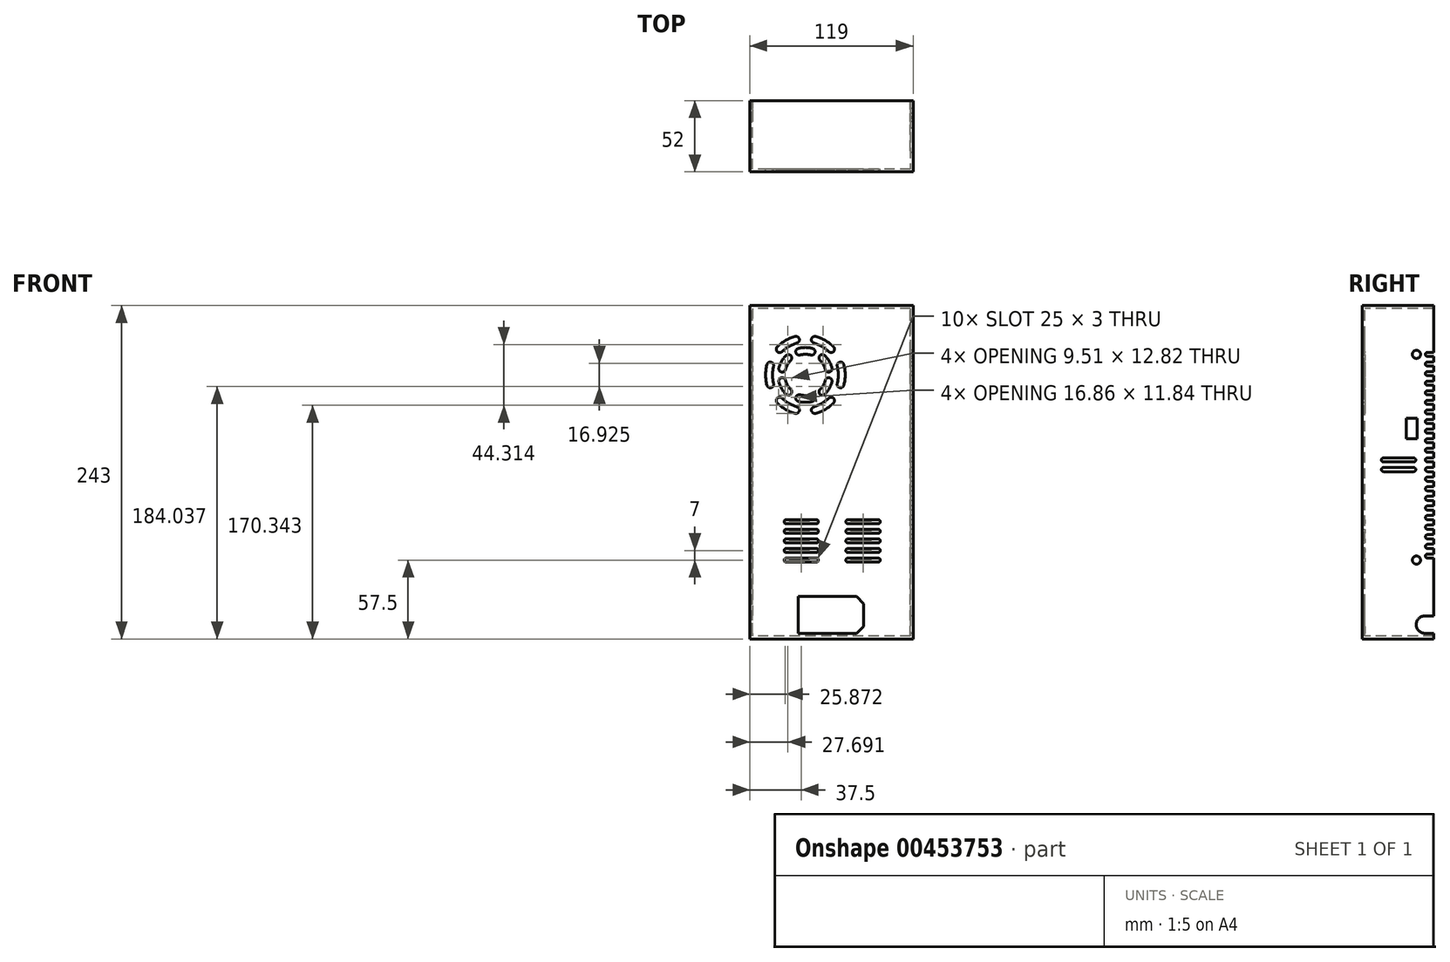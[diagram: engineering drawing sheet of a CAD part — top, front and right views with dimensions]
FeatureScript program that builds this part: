
annotation { "Feature Type Name" : "Feature", "Feature Type Description" : "" }
export const myFeature = defineFeature(function(context is Context, id is Id, definition is map)
    precondition{}
    {
        {
            assignVariable(context, id + "F0", {"name" : "Thickness", "anyValue" : 2});
        }
        {
            var Q0;
            Q0=qCreatedBy(makeId("Front.planeOp"),FACE);
            var sketch = newSketch(context, id + "F1", { "sketchPlane" : qUnion([Q0])});
            skLineSegment(sketch, "E0.bottom", {"start": v(57.5, -120.5) * mm, "end": v(-57.5, -120.5) * mm});
            skLineSegment(sketch, "E0.top", {"start": v(57.5, 120.5) * mm, "end": v(-57.5, 120.5) * mm});
            skLineSegment(sketch, "E0.left", {"start": v(57.5, -120.5) * mm, "end": v(57.5, 120.5) * mm});
            skLineSegment(sketch, "E0.right", {"start": v(-57.5, -120.5) * mm, "end": v(-57.5, 120.5) * mm});
            skPoint(sketch, "E0.middle", {"position": v(0, 0) * mm});
            skLineSegment(sketch, "E1.bottom", {"start": v(18.15, -116.5) * mm, "end": v(-24.1, -116.5) * mm});
            skLineSegment(sketch, "E1.top", {"start": v(18.15, -89.5) * mm, "end": v(-24.1, -89.5) * mm});
            skLineSegment(sketch, "E1.left", {"start": v(23.4, -111.25) * mm, "end": v(23.4, -94.75) * mm});
            skLineSegment(sketch, "E1.right", {"start": v(-24.1, -116.5) * mm, "end": v(-24.1, -89.5) * mm});
            skLineSegment(sketch, "E2", {"start": v(23.4, -94.75) * mm, "end": v(18.15, -89.5) * mm});
            skLineSegment(sketch, "E3", {"start": v(-24.1, -103) * mm, "end": v(23.75, -103) * mm, "construction": true});
            skLineSegment(sketch, "E4.MirrorCS", {"start": v(23.4, -111.25) * mm, "end": v(18.15, -116.5) * mm});
            skPoint(sketch, "E5", {"position": v(-19, 72) * mm});
            skPoint(sketch, "E6.0.6.0", {"position": v(-23.53, 55.1) * mm});
            skPoint(sketch, "E6.0.7.0", {"position": v(-14.47, 55.1) * mm});
            skArc(sketch, "E7", {"start": v(-14.47, 55.1) * mm, "mid": v(-19, 54.5) * mm, "end": v(-23.53, 55.1) * mm, "construction": true});
            skPoint(sketch, "E8", {"position": v(-12.14, 97.6) * mm});
            skPoint(sketch, "E9.0.11.0", {"position": v(-0.26, 90.74) * mm});
            skArc(sketch, "E10", {"start": v(-12.14, 97.6) * mm, "mid": v(-5.75, 94.95) * mm, "end": v(-0.26, 90.74) * mm, "construction": true});
            skArc(sketch, "E11.1.startCap", {"start": v(-12.79, 95.18) * mm, "mid": v(-14.56, 98.24) * mm, "end": v(-11.5, 100.01) * mm});
            skArc(sketch, "E11.1.endCap", {"start": v(1.5, 92.5) * mm, "mid": v(1.5, 88.97) * mm, "end": v(-2.03, 88.97) * mm});
            skArc(sketch, "E11.1.left", {"start": v(-11.5, 100.01) * mm, "mid": v(-4.5, 97.11) * mm, "end": v(1.5, 92.5) * mm});
            skArc(sketch, "E11.1.right", {"start": v(-12.79, 95.18) * mm, "mid": v(-7, 92.78) * mm, "end": v(-2.03, 88.97) * mm});
            skArc(sketch, "E11.10.startCap", {"start": v(-15.12, 57.51) * mm, "mid": v(-12.06, 55.74) * mm, "end": v(-13.82, 52.68) * mm});
            skArc(sketch, "E11.10.endCap", {"start": v(-24.18, 52.68) * mm, "mid": v(-25.94, 55.74) * mm, "end": v(-22.88, 57.51) * mm});
            skArc(sketch, "E11.10.left", {"start": v(-13.82, 52.68) * mm, "mid": v(-19, 52) * mm, "end": v(-24.18, 52.68) * mm});
            skArc(sketch, "E11.10.right", {"start": v(-15.12, 57.51) * mm, "mid": v(-19, 57) * mm, "end": v(-22.88, 57.51) * mm});
            skLineSegment(sketch, "E12", {"start": v(-33, -35) * mm, "end": v(-11, -35) * mm, "construction": true});
            skArc(sketch, "E13.0.startCap", {"start": v(-33, -36.5) * mm, "mid": v(-34.5, -35) * mm, "end": v(-33, -33.5) * mm});
            skArc(sketch, "E13.0.endCap", {"start": v(-11, -33.5) * mm, "mid": v(-9.5, -35) * mm, "end": v(-11, -36.5) * mm});
            skLineSegment(sketch, "E13.0.left", {"start": v(-33, -33.5) * mm, "end": v(-11, -33.5) * mm});
            skLineSegment(sketch, "E13.0.right", {"start": v(-33, -36.5) * mm, "end": v(-11, -36.5) * mm});
            skLineSegment(sketch, "E14.0.1.0", {"start": v(-33, -43.5) * mm, "end": v(-11, -43.5) * mm});
            skArc(sketch, "E14.0.1.1", {"start": v(-33, -43.5) * mm, "mid": v(-34.5, -42) * mm, "end": v(-33, -40.5) * mm});
            skLineSegment(sketch, "E14.0.1.2", {"start": v(-33, -40.5) * mm, "end": v(-11, -40.5) * mm});
            skArc(sketch, "E14.0.1.3", {"start": v(-11, -40.5) * mm, "mid": v(-9.5, -42) * mm, "end": v(-11, -43.5) * mm});
            skLineSegment(sketch, "E14.0.2.0", {"start": v(-33, -50.5) * mm, "end": v(-11, -50.5) * mm});
            skArc(sketch, "E14.0.2.1", {"start": v(-33, -50.5) * mm, "mid": v(-34.5, -49) * mm, "end": v(-33, -47.5) * mm});
            skLineSegment(sketch, "E14.0.2.2", {"start": v(-33, -47.5) * mm, "end": v(-11, -47.5) * mm});
            skArc(sketch, "E14.0.2.3", {"start": v(-11, -47.5) * mm, "mid": v(-9.5, -49) * mm, "end": v(-11, -50.5) * mm});
            skLineSegment(sketch, "E14.0.3.0", {"start": v(-33, -57.5) * mm, "end": v(-11, -57.5) * mm});
            skArc(sketch, "E14.0.3.1", {"start": v(-33, -57.5) * mm, "mid": v(-34.5, -56) * mm, "end": v(-33, -54.5) * mm});
            skLineSegment(sketch, "E14.0.3.2", {"start": v(-33, -54.5) * mm, "end": v(-11, -54.5) * mm});
            skArc(sketch, "E14.0.3.3", {"start": v(-11, -54.5) * mm, "mid": v(-9.5, -56) * mm, "end": v(-11, -57.5) * mm});
            skLineSegment(sketch, "E14.0.4.0", {"start": v(-33, -64.5) * mm, "end": v(-11, -64.5) * mm});
            skArc(sketch, "E14.0.4.1", {"start": v(-33, -64.5) * mm, "mid": v(-34.5, -63) * mm, "end": v(-33, -61.5) * mm});
            skLineSegment(sketch, "E14.0.4.2", {"start": v(-33, -61.5) * mm, "end": v(-11, -61.5) * mm});
            skArc(sketch, "E14.0.4.3", {"start": v(-11, -61.5) * mm, "mid": v(-9.5, -63) * mm, "end": v(-11, -64.5) * mm});
            skLineSegment(sketch, "E14.1.0.0", {"start": v(12, -36.5) * mm, "end": v(34, -36.5) * mm});
            skArc(sketch, "E14.1.0.1", {"start": v(12, -36.5) * mm, "mid": v(10.5, -35) * mm, "end": v(12, -33.5) * mm});
            skLineSegment(sketch, "E14.1.0.2", {"start": v(12, -33.5) * mm, "end": v(34, -33.5) * mm});
            skArc(sketch, "E14.1.0.3", {"start": v(34, -33.5) * mm, "mid": v(35.5, -35) * mm, "end": v(34, -36.5) * mm});
            skLineSegment(sketch, "E14.1.1.0", {"start": v(12, -43.5) * mm, "end": v(34, -43.5) * mm});
            skArc(sketch, "E14.1.1.1", {"start": v(12, -43.5) * mm, "mid": v(10.5, -42) * mm, "end": v(12, -40.5) * mm});
            skLineSegment(sketch, "E14.1.1.2", {"start": v(12, -40.5) * mm, "end": v(34, -40.5) * mm});
            skArc(sketch, "E14.1.1.3", {"start": v(34, -40.5) * mm, "mid": v(35.5, -42) * mm, "end": v(34, -43.5) * mm});
            skLineSegment(sketch, "E14.1.2.0", {"start": v(12, -50.5) * mm, "end": v(34, -50.5) * mm});
            skArc(sketch, "E14.1.2.1", {"start": v(12, -50.5) * mm, "mid": v(10.5, -49) * mm, "end": v(12, -47.5) * mm});
            skLineSegment(sketch, "E14.1.2.2", {"start": v(12, -47.5) * mm, "end": v(34, -47.5) * mm});
            skArc(sketch, "E14.1.2.3", {"start": v(34, -47.5) * mm, "mid": v(35.5, -49) * mm, "end": v(34, -50.5) * mm});
            skLineSegment(sketch, "E14.1.3.0", {"start": v(12, -57.5) * mm, "end": v(34, -57.5) * mm});
            skArc(sketch, "E14.1.3.1", {"start": v(12, -57.5) * mm, "mid": v(10.5, -56) * mm, "end": v(12, -54.5) * mm});
            skLineSegment(sketch, "E14.1.3.2", {"start": v(12, -54.5) * mm, "end": v(34, -54.5) * mm});
            skArc(sketch, "E14.1.3.3", {"start": v(34, -54.5) * mm, "mid": v(35.5, -56) * mm, "end": v(34, -57.5) * mm});
            skLineSegment(sketch, "E14.1.4.0", {"start": v(12, -64.5) * mm, "end": v(34, -64.5) * mm});
            skArc(sketch, "E14.1.4.1", {"start": v(12, -64.5) * mm, "mid": v(10.5, -63) * mm, "end": v(12, -61.5) * mm});
            skLineSegment(sketch, "E14.1.4.2", {"start": v(12, -61.5) * mm, "end": v(34, -61.5) * mm});
            skArc(sketch, "E14.1.4.3", {"start": v(34, -61.5) * mm, "mid": v(35.5, -63) * mm, "end": v(34, -64.5) * mm});
            skLineSegment(sketch, "E14.direction1", {"start": v(-33, -36.5) * mm, "end": v(12, -36.5) * mm, "construction": true});
            skLineSegment(sketch, "E14.direction2", {"start": v(-33, -36.5) * mm, "end": v(-33, -43.5) * mm, "construction": true});
            skLineSegment(sketch, "E15", {"start": v(-19, 72) * mm, "end": v(-12.14, 97.6) * mm, "construction": true});
            skLineSegment(sketch, "E16", {"start": v(-19, 72) * mm, "end": v(-19, 89.5) * mm, "construction": true});
            skLineSegment(sketch, "E17", {"start": v(-19, 72) * mm, "end": v(-0.26, 90.74) * mm, "construction": true});
            skLineSegment(sketch, "E18", {"start": v(-19, 72) * mm, "end": v(-14.47, 55.1) * mm, "construction": true});
            skLineSegment(sketch, "E19", {"start": v(-19, 72) * mm, "end": v(-23.53, 55.1) * mm, "construction": true});
            skLineSegment(sketch, "E20", {"start": v(-19, 72) * mm, "end": v(-19, 54.5) * mm, "construction": true});
            skArc(sketch, "E21.1.0", {"start": v(-39.5, 92.5) * mm, "mid": v(-33.5, 97.11) * mm, "end": v(-26.5, 100.01) * mm});
            skArc(sketch, "E21.1.1", {"start": v(-26.5, 100.01) * mm, "mid": v(-23.44, 98.24) * mm, "end": v(-25.21, 95.18) * mm});
            skArc(sketch, "E21.1.2", {"start": v(-35.97, 88.97) * mm, "mid": v(-31, 92.78) * mm, "end": v(-25.21, 95.18) * mm});
            skArc(sketch, "E21.1.3", {"start": v(-35.97, 88.97) * mm, "mid": v(-39.5, 88.97) * mm, "end": v(-39.5, 92.5) * mm});
            skArc(sketch, "E21.1.4", {"start": v(-4.51, 68.12) * mm, "mid": v(-6, 64.5) * mm, "end": v(-8.4, 61.4) * mm});
            skArc(sketch, "E21.1.5", {"start": v(0.32, 66.82) * mm, "mid": v(-1.68, 62) * mm, "end": v(-4.86, 57.86) * mm});
            skArc(sketch, "E21.1.6", {"start": v(-4.86, 57.86) * mm, "mid": v(-8.4, 57.86) * mm, "end": v(-8.4, 61.4) * mm});
            skArc(sketch, "E21.1.7", {"start": v(-4.51, 68.12) * mm, "mid": v(-1.45, 69.89) * mm, "end": v(0.32, 66.82) * mm});
            skArc(sketch, "E21.2.0", {"start": v(-47.01, 64.5) * mm, "mid": v(-48, 72) * mm, "end": v(-47.01, 79.5) * mm});
            skArc(sketch, "E21.2.1", {"start": v(-47.01, 79.5) * mm, "mid": v(-43.95, 81.27) * mm, "end": v(-42.18, 78.21) * mm});
            skArc(sketch, "E21.2.2", {"start": v(-42.18, 65.79) * mm, "mid": v(-43, 72) * mm, "end": v(-42.18, 78.21) * mm});
            skArc(sketch, "E21.2.3", {"start": v(-42.18, 65.79) * mm, "mid": v(-43.95, 62.73) * mm, "end": v(-47.01, 64.5) * mm});
            skArc(sketch, "E21.2.4", {"start": v(-8.4, 82.6) * mm, "mid": v(-6, 79.5) * mm, "end": v(-4.51, 75.88) * mm});
            skArc(sketch, "E21.2.5", {"start": v(-4.86, 86.14) * mm, "mid": v(-1.68, 82) * mm, "end": v(0.32, 77.18) * mm});
            skArc(sketch, "E21.2.6", {"start": v(0.32, 77.18) * mm, "mid": v(-1.45, 74.11) * mm, "end": v(-4.51, 75.88) * mm});
            skArc(sketch, "E21.2.7", {"start": v(-8.4, 82.6) * mm, "mid": v(-8.4, 86.14) * mm, "end": v(-4.86, 86.14) * mm});
            skArc(sketch, "E21.3.0", {"start": v(-26.5, 43.99) * mm, "mid": v(-33.5, 46.89) * mm, "end": v(-39.5, 51.5) * mm});
            skArc(sketch, "E21.3.1", {"start": v(-39.5, 51.5) * mm, "mid": v(-39.5, 55.03) * mm, "end": v(-35.97, 55.03) * mm});
            skArc(sketch, "E21.3.2", {"start": v(-25.21, 48.82) * mm, "mid": v(-31, 51.22) * mm, "end": v(-35.97, 55.03) * mm});
            skArc(sketch, "E21.3.3", {"start": v(-25.21, 48.82) * mm, "mid": v(-23.44, 45.76) * mm, "end": v(-26.5, 43.99) * mm});
            skArc(sketch, "E21.3.4", {"start": v(-22.88, 86.49) * mm, "mid": v(-19, 87) * mm, "end": v(-15.12, 86.49) * mm});
            skArc(sketch, "E21.3.5", {"start": v(-24.18, 91.32) * mm, "mid": v(-19, 92) * mm, "end": v(-13.82, 91.32) * mm});
            skArc(sketch, "E21.3.6", {"start": v(-13.82, 91.32) * mm, "mid": v(-12.06, 88.26) * mm, "end": v(-15.12, 86.49) * mm});
            skArc(sketch, "E21.3.7", {"start": v(-22.88, 86.49) * mm, "mid": v(-25.94, 88.26) * mm, "end": v(-24.18, 91.32) * mm});
            skArc(sketch, "E21.4.0", {"start": v(1.5, 51.5) * mm, "mid": v(-4.5, 46.89) * mm, "end": v(-11.5, 43.99) * mm});
            skArc(sketch, "E21.4.1", {"start": v(-11.5, 43.99) * mm, "mid": v(-14.56, 45.76) * mm, "end": v(-12.79, 48.82) * mm});
            skArc(sketch, "E21.4.2", {"start": v(-2.03, 55.03) * mm, "mid": v(-7, 51.22) * mm, "end": v(-12.79, 48.82) * mm});
            skArc(sketch, "E21.4.3", {"start": v(-2.03, 55.03) * mm, "mid": v(1.5, 55.03) * mm, "end": v(1.5, 51.5) * mm});
            skArc(sketch, "E21.4.4", {"start": v(-33.49, 75.88) * mm, "mid": v(-32, 79.5) * mm, "end": v(-29.6, 82.6) * mm});
            skArc(sketch, "E21.4.5", {"start": v(-38.32, 77.18) * mm, "mid": v(-36.32, 82) * mm, "end": v(-33.14, 86.14) * mm});
            skArc(sketch, "E21.4.6", {"start": v(-33.14, 86.14) * mm, "mid": v(-29.6, 86.14) * mm, "end": v(-29.6, 82.6) * mm});
            skArc(sketch, "E21.4.7", {"start": v(-33.49, 75.88) * mm, "mid": v(-36.55, 74.11) * mm, "end": v(-38.32, 77.18) * mm});
            skArc(sketch, "E21.5.0", {"start": v(9.01, 79.5) * mm, "mid": v(10, 72) * mm, "end": v(9.01, 64.5) * mm});
            skArc(sketch, "E21.5.1", {"start": v(9.01, 64.5) * mm, "mid": v(5.95, 62.73) * mm, "end": v(4.18, 65.79) * mm});
            skArc(sketch, "E21.5.2", {"start": v(4.18, 78.21) * mm, "mid": v(5, 72) * mm, "end": v(4.18, 65.79) * mm});
            skArc(sketch, "E21.5.3", {"start": v(4.18, 78.21) * mm, "mid": v(5.95, 81.27) * mm, "end": v(9.01, 79.5) * mm});
            skArc(sketch, "E21.5.4", {"start": v(-29.6, 61.4) * mm, "mid": v(-32, 64.5) * mm, "end": v(-33.49, 68.12) * mm});
            skArc(sketch, "E21.5.5", {"start": v(-33.14, 57.86) * mm, "mid": v(-36.32, 62) * mm, "end": v(-38.32, 66.82) * mm});
            skArc(sketch, "E21.5.6", {"start": v(-38.32, 66.82) * mm, "mid": v(-36.55, 69.89) * mm, "end": v(-33.49, 68.12) * mm});
            skArc(sketch, "E21.5.7", {"start": v(-29.6, 61.4) * mm, "mid": v(-29.6, 57.86) * mm, "end": v(-33.14, 57.86) * mm});
            skSolve(sketch);
        }
        {
            var Q0;
            Q0=makeQuery(id+"F1.imprint","IMPRINT",FACE,{"disambiguationData":[TD([[makeQuery(id+"F1.imprint","IMPRINT",EDGE,{"derivedFrom":sQuery(id+"F1.wireOp",EDGE,"E0.bottom")}),-1.0]])]});
            extrude(context, id + "F2", {"entities" : qUnion([Q0]), "depth" : (getVariable(context, 'Thickness')) * mm});
        }
        {
            var Q0;
            Q0=makeQuery(id+"F2.opExtrude","SWEPT_FACE",FACE,{"disambiguationData":[OSD([sQuery(id+"F1.wireOp",EDGE,"E0.left")])]});
            var sketch = newSketch(context, id + "F3", { "sketchPlane" : qUnion([Q0])});
            skLineSegment(sketch, "E22.bottom", {"start": v(50, 120.5) * mm, "end": v(-2, 120.5) * mm});
            skLineSegment(sketch, "E22.top", {"start": v(50, -120.5) * mm, "end": v(-2, -120.5) * mm});
            skLineSegment(sketch, "E22.left", {"start": v(50, 120.5) * mm, "end": v(50, -120.5) * mm});
            skLineSegment(sketch, "E22.right", {"start": v(-2, 120.5) * mm, "end": v(-2, -120.5) * mm});
            skCircle(sketch, "E23", {"center": v(37.5, 87) * mm, "radius": 3 * mm});
            skCircle(sketch, "E24", {"center": v(37.5, -63) * mm, "radius": 3 * mm});
            skLineSegment(sketch, "E25.bottom", {"start": v(38, 40.5) * mm, "end": v(30, 40.5) * mm});
            skLineSegment(sketch, "E25.top", {"start": v(38, 25.5) * mm, "end": v(30, 25.5) * mm});
            skLineSegment(sketch, "E25.left", {"start": v(38, 40.5) * mm, "end": v(38, 25.5) * mm});
            skLineSegment(sketch, "E25.right", {"start": v(30, 40.5) * mm, "end": v(30, 25.5) * mm});
            skLineSegment(sketch, "E26", {"start": v(50, -120.5) * mm, "end": v(50, -120.5) * mm});
            skPoint(sketch, "E27", {"position": v(50, -110) * mm});
            skLineSegment(sketch, "E28", {"start": v(43.65, -103.65) * mm, "end": v(50, -103.65) * mm});
            skLineSegment(sketch, "E29", {"start": v(43.65, -116.35) * mm, "end": v(50, -116.35) * mm});
            skArc(sketch, "E30", {"start": v(43.65, -103.65) * mm, "mid": v(37.3, -110) * mm, "end": v(43.65, -116.35) * mm});
            skArc(sketch, "E31", {"start": v(43.65, -116.35) * mm, "mid": v(50, -110) * mm, "end": v(43.65, -103.65) * mm, "construction": true});
            skLineSegment(sketch, "E32", {"start": v(13.5, 10) * mm, "end": v(35.5, 10) * mm});
            skArc(sketch, "E33.0.startCap", {"start": v(13.5, 8.5) * mm, "mid": v(12, 10) * mm, "end": v(13.5, 11.5) * mm});
            skArc(sketch, "E33.0.endCap", {"start": v(35.5, 11.5) * mm, "mid": v(37, 10) * mm, "end": v(35.5, 8.5) * mm});
            skLineSegment(sketch, "E33.0.left", {"start": v(13.5, 11.5) * mm, "end": v(35.5, 11.5) * mm});
            skLineSegment(sketch, "E33.0.right", {"start": v(13.5, 8.5) * mm, "end": v(35.5, 8.5) * mm});
            skLineSegment(sketch, "E34.0.1.0", {"start": v(13.5, 4.5) * mm, "end": v(35.5, 4.5) * mm});
            skLineSegment(sketch, "E34.0.1.1", {"start": v(13.5, 1.5) * mm, "end": v(35.5, 1.5) * mm});
            skArc(sketch, "E34.0.1.2", {"start": v(13.5, 1.5) * mm, "mid": v(12, 3) * mm, "end": v(13.5, 4.5) * mm});
            skArc(sketch, "E34.0.1.3", {"start": v(35.5, 4.5) * mm, "mid": v(37, 3) * mm, "end": v(35.5, 1.5) * mm});
            skLineSegment(sketch, "E34.direction1", {"start": v(13.5, 11.5) * mm, "end": v(35.5, 11.5) * mm, "construction": true});
            skLineSegment(sketch, "E34.direction2", {"start": v(13.5, 11.5) * mm, "end": v(13.5, 4.5) * mm, "construction": true});
            skLineSegment(sketch, "E35", {"start": v(50, 87) * mm, "end": v(45.5, 87) * mm, "construction": true});
            skArc(sketch, "E36.0.endCap", {"start": v(45.5, 85.5) * mm, "mid": v(44, 87) * mm, "end": v(45.5, 88.5) * mm});
            skLineSegment(sketch, "E36.0.left", {"start": v(50, 85.5) * mm, "end": v(45.5, 85.5) * mm});
            skLineSegment(sketch, "E36.0.right", {"start": v(50, 88.5) * mm, "end": v(45.5, 88.5) * mm});
            skLineSegment(sketch, "E37.0.1.0", {"start": v(50, 81.5) * mm, "end": v(45.5, 81.5) * mm});
            skLineSegment(sketch, "E37.0.1.1", {"start": v(50, 78.5) * mm, "end": v(45.5, 78.5) * mm});
            skArc(sketch, "E37.0.1.2", {"start": v(45.5, 78.5) * mm, "mid": v(44, 80) * mm, "end": v(45.5, 81.5) * mm});
            skLineSegment(sketch, "E37.0.2.0", {"start": v(50, 74.5) * mm, "end": v(45.5, 74.5) * mm});
            skLineSegment(sketch, "E37.0.2.1", {"start": v(50, 71.5) * mm, "end": v(45.5, 71.5) * mm});
            skArc(sketch, "E37.0.2.2", {"start": v(45.5, 71.5) * mm, "mid": v(44, 73) * mm, "end": v(45.5, 74.5) * mm});
            skLineSegment(sketch, "E37.0.3.0", {"start": v(50, 67.5) * mm, "end": v(45.5, 67.5) * mm});
            skLineSegment(sketch, "E37.0.3.1", {"start": v(50, 64.5) * mm, "end": v(45.5, 64.5) * mm});
            skArc(sketch, "E37.0.3.2", {"start": v(45.5, 64.5) * mm, "mid": v(44, 66) * mm, "end": v(45.5, 67.5) * mm});
            skLineSegment(sketch, "E37.0.4.0", {"start": v(50, 60.5) * mm, "end": v(45.5, 60.5) * mm});
            skLineSegment(sketch, "E37.0.4.1", {"start": v(50, 57.5) * mm, "end": v(45.5, 57.5) * mm});
            skArc(sketch, "E37.0.4.2", {"start": v(45.5, 57.5) * mm, "mid": v(44, 59) * mm, "end": v(45.5, 60.5) * mm});
            skLineSegment(sketch, "E37.0.5.0", {"start": v(50, 53.5) * mm, "end": v(45.5, 53.5) * mm});
            skLineSegment(sketch, "E37.0.5.1", {"start": v(50, 50.5) * mm, "end": v(45.5, 50.5) * mm});
            skArc(sketch, "E37.0.5.2", {"start": v(45.5, 50.5) * mm, "mid": v(44, 52) * mm, "end": v(45.5, 53.5) * mm});
            skLineSegment(sketch, "E37.0.6.0", {"start": v(50, 46.5) * mm, "end": v(45.5, 46.5) * mm});
            skLineSegment(sketch, "E37.0.6.1", {"start": v(50, 43.5) * mm, "end": v(45.5, 43.5) * mm});
            skArc(sketch, "E37.0.6.2", {"start": v(45.5, 43.5) * mm, "mid": v(44, 45) * mm, "end": v(45.5, 46.5) * mm});
            skLineSegment(sketch, "E37.0.7.0", {"start": v(50, 39.5) * mm, "end": v(45.5, 39.5) * mm});
            skLineSegment(sketch, "E37.0.7.1", {"start": v(50, 36.5) * mm, "end": v(45.5, 36.5) * mm});
            skArc(sketch, "E37.0.7.2", {"start": v(45.5, 36.5) * mm, "mid": v(44, 38) * mm, "end": v(45.5, 39.5) * mm});
            skLineSegment(sketch, "E37.0.8.0", {"start": v(50, 32.5) * mm, "end": v(45.5, 32.5) * mm});
            skLineSegment(sketch, "E37.0.8.1", {"start": v(50, 29.5) * mm, "end": v(45.5, 29.5) * mm});
            skArc(sketch, "E37.0.8.2", {"start": v(45.5, 29.5) * mm, "mid": v(44, 31) * mm, "end": v(45.5, 32.5) * mm});
            skLineSegment(sketch, "E37.0.9.0", {"start": v(50, 25.5) * mm, "end": v(45.5, 25.5) * mm});
            skLineSegment(sketch, "E37.0.9.1", {"start": v(50, 22.5) * mm, "end": v(45.5, 22.5) * mm});
            skArc(sketch, "E37.0.9.2", {"start": v(45.5, 22.5) * mm, "mid": v(44, 24) * mm, "end": v(45.5, 25.5) * mm});
            skLineSegment(sketch, "E37.0.10.0", {"start": v(50, 18.5) * mm, "end": v(45.5, 18.5) * mm});
            skLineSegment(sketch, "E37.0.10.1", {"start": v(50, 15.5) * mm, "end": v(45.5, 15.5) * mm});
            skArc(sketch, "E37.0.10.2", {"start": v(45.5, 15.5) * mm, "mid": v(44, 17) * mm, "end": v(45.5, 18.5) * mm});
            skLineSegment(sketch, "E37.0.11.0", {"start": v(50, 11.5) * mm, "end": v(45.5, 11.5) * mm});
            skLineSegment(sketch, "E37.0.11.1", {"start": v(50, 8.5) * mm, "end": v(45.5, 8.5) * mm});
            skArc(sketch, "E37.0.11.2", {"start": v(45.5, 8.5) * mm, "mid": v(44, 10) * mm, "end": v(45.5, 11.5) * mm});
            skLineSegment(sketch, "E37.0.12.0", {"start": v(50, 4.5) * mm, "end": v(45.5, 4.5) * mm});
            skLineSegment(sketch, "E37.0.12.1", {"start": v(50, 1.5) * mm, "end": v(45.5, 1.5) * mm});
            skArc(sketch, "E37.0.12.2", {"start": v(45.5, 1.5) * mm, "mid": v(44, 3) * mm, "end": v(45.5, 4.5) * mm});
            skLineSegment(sketch, "E37.0.13.0", {"start": v(50, -2.5) * mm, "end": v(45.5, -2.5) * mm});
            skLineSegment(sketch, "E37.0.13.1", {"start": v(50, -5.5) * mm, "end": v(45.5, -5.5) * mm});
            skArc(sketch, "E37.0.13.2", {"start": v(45.5, -5.5) * mm, "mid": v(44, -4) * mm, "end": v(45.5, -2.5) * mm});
            skLineSegment(sketch, "E37.0.14.0", {"start": v(50, -9.5) * mm, "end": v(45.5, -9.5) * mm});
            skLineSegment(sketch, "E37.0.14.1", {"start": v(50, -12.5) * mm, "end": v(45.5, -12.5) * mm});
            skArc(sketch, "E37.0.14.2", {"start": v(45.5, -12.5) * mm, "mid": v(44, -11) * mm, "end": v(45.5, -9.5) * mm});
            skLineSegment(sketch, "E37.0.15.0", {"start": v(50, -16.5) * mm, "end": v(45.5, -16.5) * mm});
            skLineSegment(sketch, "E37.0.15.1", {"start": v(50, -19.5) * mm, "end": v(45.5, -19.5) * mm});
            skArc(sketch, "E37.0.15.2", {"start": v(45.5, -19.5) * mm, "mid": v(44, -18) * mm, "end": v(45.5, -16.5) * mm});
            skLineSegment(sketch, "E37.0.16.0", {"start": v(50, -23.5) * mm, "end": v(45.5, -23.5) * mm});
            skLineSegment(sketch, "E37.0.16.1", {"start": v(50, -26.5) * mm, "end": v(45.5, -26.5) * mm});
            skArc(sketch, "E37.0.16.2", {"start": v(45.5, -26.5) * mm, "mid": v(44, -25) * mm, "end": v(45.5, -23.5) * mm});
            skLineSegment(sketch, "E37.0.17.0", {"start": v(50, -30.5) * mm, "end": v(45.5, -30.5) * mm});
            skLineSegment(sketch, "E37.0.17.1", {"start": v(50, -33.5) * mm, "end": v(45.5, -33.5) * mm});
            skArc(sketch, "E37.0.17.2", {"start": v(45.5, -33.5) * mm, "mid": v(44, -32) * mm, "end": v(45.5, -30.5) * mm});
            skLineSegment(sketch, "E37.0.18.0", {"start": v(50, -37.5) * mm, "end": v(45.5, -37.5) * mm});
            skLineSegment(sketch, "E37.0.18.1", {"start": v(50, -40.5) * mm, "end": v(45.5, -40.5) * mm});
            skArc(sketch, "E37.0.18.2", {"start": v(45.5, -40.5) * mm, "mid": v(44, -39) * mm, "end": v(45.5, -37.5) * mm});
            skLineSegment(sketch, "E37.0.19.0", {"start": v(50, -44.5) * mm, "end": v(45.5, -44.5) * mm});
            skLineSegment(sketch, "E37.0.19.1", {"start": v(50, -47.5) * mm, "end": v(45.5, -47.5) * mm});
            skArc(sketch, "E37.0.19.2", {"start": v(45.5, -47.5) * mm, "mid": v(44, -46) * mm, "end": v(45.5, -44.5) * mm});
            skLineSegment(sketch, "E37.0.20.0", {"start": v(50, -51.5) * mm, "end": v(45.5, -51.5) * mm});
            skLineSegment(sketch, "E37.0.20.1", {"start": v(50, -54.5) * mm, "end": v(45.5, -54.5) * mm});
            skArc(sketch, "E37.0.20.2", {"start": v(45.5, -54.5) * mm, "mid": v(44, -53) * mm, "end": v(45.5, -51.5) * mm});
            skLineSegment(sketch, "E37.0.21.0", {"start": v(50, -58.5) * mm, "end": v(45.5, -58.5) * mm});
            skLineSegment(sketch, "E37.0.21.1", {"start": v(50, -61.5) * mm, "end": v(45.5, -61.5) * mm});
            skArc(sketch, "E37.0.21.2", {"start": v(45.5, -61.5) * mm, "mid": v(44, -60) * mm, "end": v(45.5, -58.5) * mm});
            skLineSegment(sketch, "E37.direction1", {"start": v(45.5, 88.5) * mm, "end": v(50, 88.5) * mm, "construction": true});
            skLineSegment(sketch, "E37.direction2", {"start": v(45.5, 88.5) * mm, "end": v(45.5, 81.5) * mm, "construction": true});
            skSolve(sketch);
        }
        {
            var Q0;
            Q0=makeQuery(id+"F3.imprint","IMPRINT",FACE,{"disambiguationData":[TD([[makeQuery(id+"F3.imprint","IMPRINT",EDGE,{"derivedFrom":sQuery(id+"F3.wireOp",EDGE,"E23")}),-1.0]])]});
            var Q1;
            {var subQ2=sQuery(id+"F3.wireOp",EDGE,"E22.right");Q1=makeQuery(id+"F3.imprint","IMPRINT",FACE,{"disambiguationData":[TD([[makeQuery(id+"F3.imprint","IMPRINT",EDGE,{"derivedFrom":subQ2}),-1.0]])]});}
            extrude(context, id + "F4", {"entities" : qUnion([Q0, Q1]), "operationType" : NewBodyOperationType.ADD, "depth" : (getVariable(context, 'Thickness')) * mm});
        }
        {
            var Q0;
            Q0=makeQuery(id+"F2.opExtrude","SWEPT_FACE",FACE,{"disambiguationData":[OSD([sQuery(id+"F1.wireOp",EDGE,"E0.right")])]});
            var sketch = newSketch(context, id + "F5", { "sketchPlane" : qUnion([Q0])});
            skLineSegment(sketch, "E38.bottom", {"start": v(2, 120.5) * mm, "end": v(-50, 120.5) * mm});
            skLineSegment(sketch, "E38.top", {"start": v(2, -120.5) * mm, "end": v(-50, -120.5) * mm});
            skLineSegment(sketch, "E38.left", {"start": v(2, 120.5) * mm, "end": v(2, -120.5) * mm});
            skLineSegment(sketch, "E38.right", {"start": v(-50, 120.5) * mm, "end": v(-50, -120.5) * mm});
            skCircle(sketch, "E39", {"center": v(-37.5, 87) * mm, "radius": 3 * mm});
            skCircle(sketch, "E40", {"center": v(-37.5, -63) * mm, "radius": 3 * mm});
            skLineSegment(sketch, "E41", {"start": v(-43.65, -116.35) * mm, "end": v(-50, -116.35) * mm});
            skLineSegment(sketch, "E42", {"start": v(-43.65, -103.65) * mm, "end": v(-50, -103.65) * mm});
            skArc(sketch, "E43", {"start": v(-43.65, -116.35) * mm, "mid": v(-37.3, -110) * mm, "end": v(-43.65, -103.65) * mm});
            skArc(sketch, "E44", {"start": v(-43.65, -103.65) * mm, "mid": v(-50, -110) * mm, "end": v(-43.65, -116.35) * mm, "construction": true});
            skLineSegment(sketch, "E45", {"start": v(-50, 87) * mm, "end": v(-45.5, 87) * mm, "construction": true});
            skArc(sketch, "E46.0.endCap", {"start": v(-45.5, 88.5) * mm, "mid": v(-44, 87) * mm, "end": v(-45.5, 85.5) * mm});
            skLineSegment(sketch, "E46.0.left", {"start": v(-50, 88.5) * mm, "end": v(-45.5, 88.5) * mm});
            skLineSegment(sketch, "E46.0.right", {"start": v(-50, 85.5) * mm, "end": v(-45.5, 85.5) * mm});
            skLineSegment(sketch, "E47.0.1.0", {"start": v(-50, 81.5) * mm, "end": v(-45.5, 81.5) * mm});
            skArc(sketch, "E47.0.1.1", {"start": v(-45.5, 81.5) * mm, "mid": v(-44, 80) * mm, "end": v(-45.5, 78.5) * mm});
            skLineSegment(sketch, "E47.0.1.2", {"start": v(-50, 78.5) * mm, "end": v(-45.5, 78.5) * mm});
            skLineSegment(sketch, "E47.0.2.0", {"start": v(-50, 74.5) * mm, "end": v(-45.5, 74.5) * mm});
            skArc(sketch, "E47.0.2.1", {"start": v(-45.5, 74.5) * mm, "mid": v(-44, 73) * mm, "end": v(-45.5, 71.5) * mm});
            skLineSegment(sketch, "E47.0.2.2", {"start": v(-50, 71.5) * mm, "end": v(-45.5, 71.5) * mm});
            skLineSegment(sketch, "E47.0.3.0", {"start": v(-50, 67.5) * mm, "end": v(-45.5, 67.5) * mm});
            skArc(sketch, "E47.0.3.1", {"start": v(-45.5, 67.5) * mm, "mid": v(-44, 66) * mm, "end": v(-45.5, 64.5) * mm});
            skLineSegment(sketch, "E47.0.3.2", {"start": v(-50, 64.5) * mm, "end": v(-45.5, 64.5) * mm});
            skLineSegment(sketch, "E47.0.4.0", {"start": v(-50, 60.5) * mm, "end": v(-45.5, 60.5) * mm});
            skArc(sketch, "E47.0.4.1", {"start": v(-45.5, 60.5) * mm, "mid": v(-44, 59) * mm, "end": v(-45.5, 57.5) * mm});
            skLineSegment(sketch, "E47.0.4.2", {"start": v(-50, 57.5) * mm, "end": v(-45.5, 57.5) * mm});
            skLineSegment(sketch, "E47.0.5.0", {"start": v(-50, 53.5) * mm, "end": v(-45.5, 53.5) * mm});
            skArc(sketch, "E47.0.5.1", {"start": v(-45.5, 53.5) * mm, "mid": v(-44, 52) * mm, "end": v(-45.5, 50.5) * mm});
            skLineSegment(sketch, "E47.0.5.2", {"start": v(-50, 50.5) * mm, "end": v(-45.5, 50.5) * mm});
            skLineSegment(sketch, "E47.0.6.0", {"start": v(-50, 46.5) * mm, "end": v(-45.5, 46.5) * mm});
            skArc(sketch, "E47.0.6.1", {"start": v(-45.5, 46.5) * mm, "mid": v(-44, 45) * mm, "end": v(-45.5, 43.5) * mm});
            skLineSegment(sketch, "E47.0.6.2", {"start": v(-50, 43.5) * mm, "end": v(-45.5, 43.5) * mm});
            skLineSegment(sketch, "E47.0.7.0", {"start": v(-50, 39.5) * mm, "end": v(-45.5, 39.5) * mm});
            skArc(sketch, "E47.0.7.1", {"start": v(-45.5, 39.5) * mm, "mid": v(-44, 38) * mm, "end": v(-45.5, 36.5) * mm});
            skLineSegment(sketch, "E47.0.7.2", {"start": v(-50, 36.5) * mm, "end": v(-45.5, 36.5) * mm});
            skLineSegment(sketch, "E47.0.8.0", {"start": v(-50, 32.5) * mm, "end": v(-45.5, 32.5) * mm});
            skArc(sketch, "E47.0.8.1", {"start": v(-45.5, 32.5) * mm, "mid": v(-44, 31) * mm, "end": v(-45.5, 29.5) * mm});
            skLineSegment(sketch, "E47.0.8.2", {"start": v(-50, 29.5) * mm, "end": v(-45.5, 29.5) * mm});
            skLineSegment(sketch, "E47.0.9.0", {"start": v(-50, 25.5) * mm, "end": v(-45.5, 25.5) * mm});
            skArc(sketch, "E47.0.9.1", {"start": v(-45.5, 25.5) * mm, "mid": v(-44, 24) * mm, "end": v(-45.5, 22.5) * mm});
            skLineSegment(sketch, "E47.0.9.2", {"start": v(-50, 22.5) * mm, "end": v(-45.5, 22.5) * mm});
            skLineSegment(sketch, "E47.0.10.0", {"start": v(-50, 18.5) * mm, "end": v(-45.5, 18.5) * mm});
            skArc(sketch, "E47.0.10.1", {"start": v(-45.5, 18.5) * mm, "mid": v(-44, 17) * mm, "end": v(-45.5, 15.5) * mm});
            skLineSegment(sketch, "E47.0.10.2", {"start": v(-50, 15.5) * mm, "end": v(-45.5, 15.5) * mm});
            skLineSegment(sketch, "E47.0.11.0", {"start": v(-50, 11.5) * mm, "end": v(-45.5, 11.5) * mm});
            skArc(sketch, "E47.0.11.1", {"start": v(-45.5, 11.5) * mm, "mid": v(-44, 10) * mm, "end": v(-45.5, 8.5) * mm});
            skLineSegment(sketch, "E47.0.11.2", {"start": v(-50, 8.5) * mm, "end": v(-45.5, 8.5) * mm});
            skLineSegment(sketch, "E47.0.12.0", {"start": v(-50, 4.5) * mm, "end": v(-45.5, 4.5) * mm});
            skArc(sketch, "E47.0.12.1", {"start": v(-45.5, 4.5) * mm, "mid": v(-44, 3) * mm, "end": v(-45.5, 1.5) * mm});
            skLineSegment(sketch, "E47.0.12.2", {"start": v(-50, 1.5) * mm, "end": v(-45.5, 1.5) * mm});
            skLineSegment(sketch, "E47.0.13.0", {"start": v(-50, -2.5) * mm, "end": v(-45.5, -2.5) * mm});
            skArc(sketch, "E47.0.13.1", {"start": v(-45.5, -2.5) * mm, "mid": v(-44, -4) * mm, "end": v(-45.5, -5.5) * mm});
            skLineSegment(sketch, "E47.0.13.2", {"start": v(-50, -5.5) * mm, "end": v(-45.5, -5.5) * mm});
            skLineSegment(sketch, "E47.0.14.0", {"start": v(-50, -9.5) * mm, "end": v(-45.5, -9.5) * mm});
            skArc(sketch, "E47.0.14.1", {"start": v(-45.5, -9.5) * mm, "mid": v(-44, -11) * mm, "end": v(-45.5, -12.5) * mm});
            skLineSegment(sketch, "E47.0.14.2", {"start": v(-50, -12.5) * mm, "end": v(-45.5, -12.5) * mm});
            skLineSegment(sketch, "E47.0.15.0", {"start": v(-50, -16.5) * mm, "end": v(-45.5, -16.5) * mm});
            skArc(sketch, "E47.0.15.1", {"start": v(-45.5, -16.5) * mm, "mid": v(-44, -18) * mm, "end": v(-45.5, -19.5) * mm});
            skLineSegment(sketch, "E47.0.15.2", {"start": v(-50, -19.5) * mm, "end": v(-45.5, -19.5) * mm});
            skLineSegment(sketch, "E47.0.16.0", {"start": v(-50, -23.5) * mm, "end": v(-45.5, -23.5) * mm});
            skArc(sketch, "E47.0.16.1", {"start": v(-45.5, -23.5) * mm, "mid": v(-44, -25) * mm, "end": v(-45.5, -26.5) * mm});
            skLineSegment(sketch, "E47.0.16.2", {"start": v(-50, -26.5) * mm, "end": v(-45.5, -26.5) * mm});
            skLineSegment(sketch, "E47.0.17.0", {"start": v(-50, -30.5) * mm, "end": v(-45.5, -30.5) * mm});
            skArc(sketch, "E47.0.17.1", {"start": v(-45.5, -30.5) * mm, "mid": v(-44, -32) * mm, "end": v(-45.5, -33.5) * mm});
            skLineSegment(sketch, "E47.0.17.2", {"start": v(-50, -33.5) * mm, "end": v(-45.5, -33.5) * mm});
            skLineSegment(sketch, "E47.0.18.0", {"start": v(-50, -37.5) * mm, "end": v(-45.5, -37.5) * mm});
            skArc(sketch, "E47.0.18.1", {"start": v(-45.5, -37.5) * mm, "mid": v(-44, -39) * mm, "end": v(-45.5, -40.5) * mm});
            skLineSegment(sketch, "E47.0.18.2", {"start": v(-50, -40.5) * mm, "end": v(-45.5, -40.5) * mm});
            skLineSegment(sketch, "E47.0.19.0", {"start": v(-50, -44.5) * mm, "end": v(-45.5, -44.5) * mm});
            skArc(sketch, "E47.0.19.1", {"start": v(-45.5, -44.5) * mm, "mid": v(-44, -46) * mm, "end": v(-45.5, -47.5) * mm});
            skLineSegment(sketch, "E47.0.19.2", {"start": v(-50, -47.5) * mm, "end": v(-45.5, -47.5) * mm});
            skLineSegment(sketch, "E47.0.20.0", {"start": v(-50, -51.5) * mm, "end": v(-45.5, -51.5) * mm});
            skArc(sketch, "E47.0.20.1", {"start": v(-45.5, -51.5) * mm, "mid": v(-44, -53) * mm, "end": v(-45.5, -54.5) * mm});
            skLineSegment(sketch, "E47.0.20.2", {"start": v(-50, -54.5) * mm, "end": v(-45.5, -54.5) * mm});
            skLineSegment(sketch, "E47.0.21.0", {"start": v(-50, -58.5) * mm, "end": v(-45.5, -58.5) * mm});
            skArc(sketch, "E47.0.21.1", {"start": v(-45.5, -58.5) * mm, "mid": v(-44, -60) * mm, "end": v(-45.5, -61.5) * mm});
            skLineSegment(sketch, "E47.0.21.2", {"start": v(-50, -61.5) * mm, "end": v(-45.5, -61.5) * mm});
            skLineSegment(sketch, "E47.direction1", {"start": v(-50, 88.5) * mm, "end": v(-50, 88.5) * mm});
            skLineSegment(sketch, "E47.direction2", {"start": v(-50, 88.5) * mm, "end": v(-50, 81.5) * mm, "construction": true});
            skSolve(sketch);
        }
        {
            var Q0;
            Q0=makeQuery(id+"F5.imprint","IMPRINT",FACE,{"disambiguationData":[TD([[makeQuery(id+"F5.imprint","IMPRINT",EDGE,{"derivedFrom":sQuery(id+"F5.wireOp",EDGE,"E38.bottom")}),1.0]])]});
            var Q1;
            {var subQ2=sQuery(id+"F5.wireOp",EDGE,"E38.right");Q1=makeQuery(id+"F5.imprint","IMPRINT",FACE,{"disambiguationData":[TD([[makeQuery(id+"F5.imprint","IMPRINT",EDGE,{"derivedFrom":subQ2}),1.0]])]});}
            extrude(context, id + "F6", {"entities" : qUnion([Q0, Q1]), "operationType" : NewBodyOperationType.ADD, "depth" : (getVariable(context, 'Thickness')) * mm});
        }
        {
            var Q0;
            Q0=makeQuery(id+"F4.boolean.opBoolean","MERGE",FACE,{"derivedFrom":[makeQuery(id+"F6.boolean.opBoolean","MERGE",FACE,{"derivedFrom":[makeQuery(id+"F2.opExtrude","SWEPT_FACE",FACE,{"disambiguationData":[OSD([sQuery(id+"F1.wireOp",EDGE,"E0.top")])]}),makeQuery(id+"F6.opExtrude","SWEPT_FACE",FACE,{"disambiguationData":[OSD([sQuery(id+"F5.wireOp",EDGE,"E38.bottom")])]})]}),makeQuery(id+"F4.opExtrude","SWEPT_FACE",FACE,{"disambiguationData":[OSD([sQuery(id+"F3.wireOp",EDGE,"E22.bottom")])]})]});
            var sketch = newSketch(context, id + "F7", { "sketchPlane" : qUnion([Q0])});
            skLineSegment(sketch, "E48.bottom", {"start": v(59.5, -2) * mm, "end": v(-59.5, -2) * mm});
            skLineSegment(sketch, "E48.top", {"start": v(59.5, 50) * mm, "end": v(-59.5, 50) * mm});
            skLineSegment(sketch, "E48.left", {"start": v(59.5, -2) * mm, "end": v(59.5, 50) * mm});
            skLineSegment(sketch, "E48.right", {"start": v(-59.5, -2) * mm, "end": v(-59.5, 50) * mm});
            skSolve(sketch);
        }
        {
            var Q0;
            Q0=makeQuery(id+"F7.imprint","IMPRINT",FACE,{"disambiguationData":[TD([[makeQuery(id+"F7.imprint","IMPRINT",EDGE,{"derivedFrom":makeQuery(id+"F2.opExtrude","CAP_EDGE",EDGE,{"disambiguationData":[OSD([sQuery(id+"F1.wireOp",EDGE,"E0.top")])],"isStart":true})}),-1.0]])]});
            var Q1;
            {var subQ1=sQuery(id+"F7.wireOp",EDGE,"E48.bottom");Q1=makeQuery(id+"F7.imprint","IMPRINT",FACE,{"disambiguationData":[TD([[makeQuery(id+"F7.imprint","IMPRINT",EDGE,{"derivedFrom":subQ1}),-1.0]])]});}
            extrude(context, id + "F8", {"entities" : qUnion([Q0, Q1]), "operationType" : NewBodyOperationType.ADD, "depth" : (getVariable(context, 'Thickness')) * mm});
        }
        {
            var Q0;
            Q0=makeQuery(id+"F4.boolean.opBoolean","MERGE",FACE,{"derivedFrom":[makeQuery(id+"F6.boolean.opBoolean","MERGE",FACE,{"derivedFrom":[makeQuery(id+"F2.opExtrude","SWEPT_FACE",FACE,{"disambiguationData":[OSD([sQuery(id+"F1.wireOp",EDGE,"E0.bottom")])]}),makeQuery(id+"F6.opExtrude","SWEPT_FACE",FACE,{"disambiguationData":[OSD([sQuery(id+"F5.wireOp",EDGE,"E38.top")])]})]}),makeQuery(id+"F4.opExtrude","SWEPT_FACE",FACE,{"disambiguationData":[OSD([sQuery(id+"F3.wireOp",EDGE,"E22.top"),sQuery(id+"F3.wireOp",EDGE,"g3eadd5Y-LM1p-6kV2-zIXE-sCsnILGw4k2A.top")])]})]});
            var sketch = newSketch(context, id + "F9", { "sketchPlane" : qUnion([Q0])});
            skLineSegment(sketch, "E49.bottom", {"start": v(59.5, 2) * mm, "end": v(-59.5, 2) * mm});
            skLineSegment(sketch, "E49.top", {"start": v(59.5, -50) * mm, "end": v(-59.5, -50) * mm});
            skLineSegment(sketch, "E49.left", {"start": v(59.5, 2) * mm, "end": v(59.5, -50) * mm});
            skLineSegment(sketch, "E49.right", {"start": v(-59.5, 2) * mm, "end": v(-59.5, -50) * mm});
            skSolve(sketch);
        }
        {
            var Q0;
            Q0=makeQuery(id+"F9.imprint","IMPRINT",FACE,{"disambiguationData":[TD([[makeQuery(id+"F9.imprint","IMPRINT",EDGE,{"derivedFrom":makeQuery(id+"F2.opExtrude","CAP_EDGE",EDGE,{"disambiguationData":[OSD([sQuery(id+"F1.wireOp",EDGE,"E0.bottom")])],"isStart":true})}),1.0]])]});
            extrude(context, id + "F10", {"entities" : qUnion([Q0]), "operationType" : NewBodyOperationType.ADD, "oppositeDirection" : true, "depth" : (getVariable(context, 'Thickness')) * mm});
        }
    });
